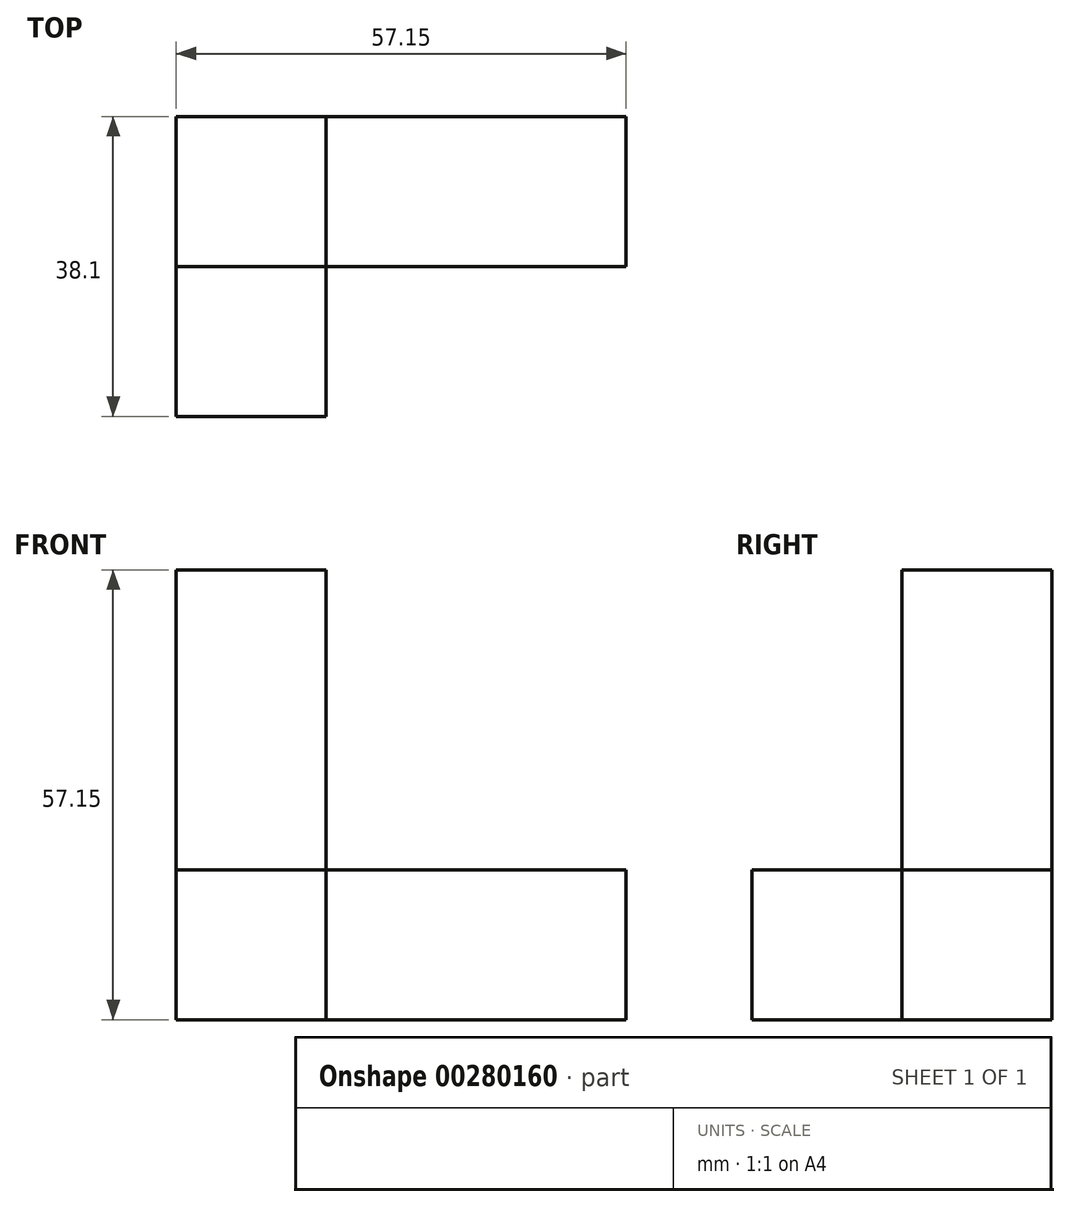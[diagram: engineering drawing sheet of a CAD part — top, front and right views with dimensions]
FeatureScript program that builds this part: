
annotation { "Feature Type Name" : "Feature", "Feature Type Description" : "" }
export const myFeature = defineFeature(function(context is Context, id is Id, definition is map)
    precondition{}
    {
        {
            var Q0;
            Q0=qCreatedBy(makeId("Front.planeOp"),FACE);
            var sketch = newSketch(context, id + "F0", { "sketchPlane" : qUnion([Q0])});
            skLineSegment(sketch, "E0.bottom", {"start": v(0, 57.15) * mm, "end": v(19.05, 57.15) * mm});
            skLineSegment(sketch, "E0.top", {"start": v(0, 0) * mm, "end": v(19.05, 0) * mm});
            skLineSegment(sketch, "E0.left", {"start": v(0, 57.15) * mm, "end": v(0, 0) * mm});
            skLineSegment(sketch, "E0.right", {"start": v(19.05, 57.15) * mm, "end": v(19.05, 0) * mm});
            skLineSegment(sketch, "E1.bottom", {"start": v(19.05, 0) * mm, "end": v(57.15, 0) * mm});
            skLineSegment(sketch, "E1.top", {"start": v(19.05, 19.05) * mm, "end": v(57.15, 19.05) * mm});
            skLineSegment(sketch, "E1.left", {"start": v(19.05, 0) * mm, "end": v(19.05, 19.05) * mm});
            skLineSegment(sketch, "E1.right", {"start": v(57.15, 0) * mm, "end": v(57.15, 19.05) * mm});
            skSolve(sketch);
        }
        {
            var Q0;
            Q0=makeQuery(id+"F0.imprint","IMPRINT",FACE,{"disambiguationData":[TD([[makeQuery(id+"F0.imprint","IMPRINT",EDGE,{"derivedFrom":sQuery(id+"F0.wireOp",EDGE,"E0.bottom")}),-1.0]])]});
            var Q1;
            Q1=makeQuery(id+"F0.imprint","IMPRINT",FACE,{"disambiguationData":[TD([[makeQuery(id+"F0.imprint","IMPRINT",EDGE,{"derivedFrom":sQuery(id+"F0.wireOp",EDGE,"E1.bottom")}),1.0]])]});
            extrude(context, id + "F1", {"entities" : qUnion([Q0, Q1]), "depth" : 19.05 * mm});
        }
        {
            var Q0;
            Q0=makeQuery(id+"F1.opExtrude","CAP_FACE",FACE,{"disambiguationData":[OSD([sQuery(id+"F0.wireOp",EDGE,"E0.bottom"),sQuery(id+"F0.wireOp",EDGE,"E0.top"),sQuery(id+"F0.wireOp",EDGE,"E0.left"),sQuery(id+"F0.wireOp",EDGE,"E0.right"),sQuery(id+"F0.wireOp",EDGE,"E1.bottom"),sQuery(id+"F0.wireOp",EDGE,"E1.top"),sQuery(id+"F0.wireOp",EDGE,"E1.right")])],"isStart":false});
            var sketch = newSketch(context, id + "F2", { "sketchPlane" : qUnion([Q0])});
            skLineSegment(sketch, "E2.bottom", {"start": v(0, 0) * mm, "end": v(19.05, 0) * mm});
            skLineSegment(sketch, "E2.top", {"start": v(0, 19.05) * mm, "end": v(19.05, 19.05) * mm});
            skLineSegment(sketch, "E2.left", {"start": v(0, 0) * mm, "end": v(0, 19.05) * mm});
            skLineSegment(sketch, "E2.right", {"start": v(19.05, 0) * mm, "end": v(19.05, 19.05) * mm});
            skSolve(sketch);
        }
        {
            var Q0;
            Q0 = qSketchRegion(id + "F2", true);
            extrude(context, id + "F3", {"entities" : qUnion([Q0]), "operationType" : NewBodyOperationType.ADD, "depth" : 19.05 * mm});
        }
    });
